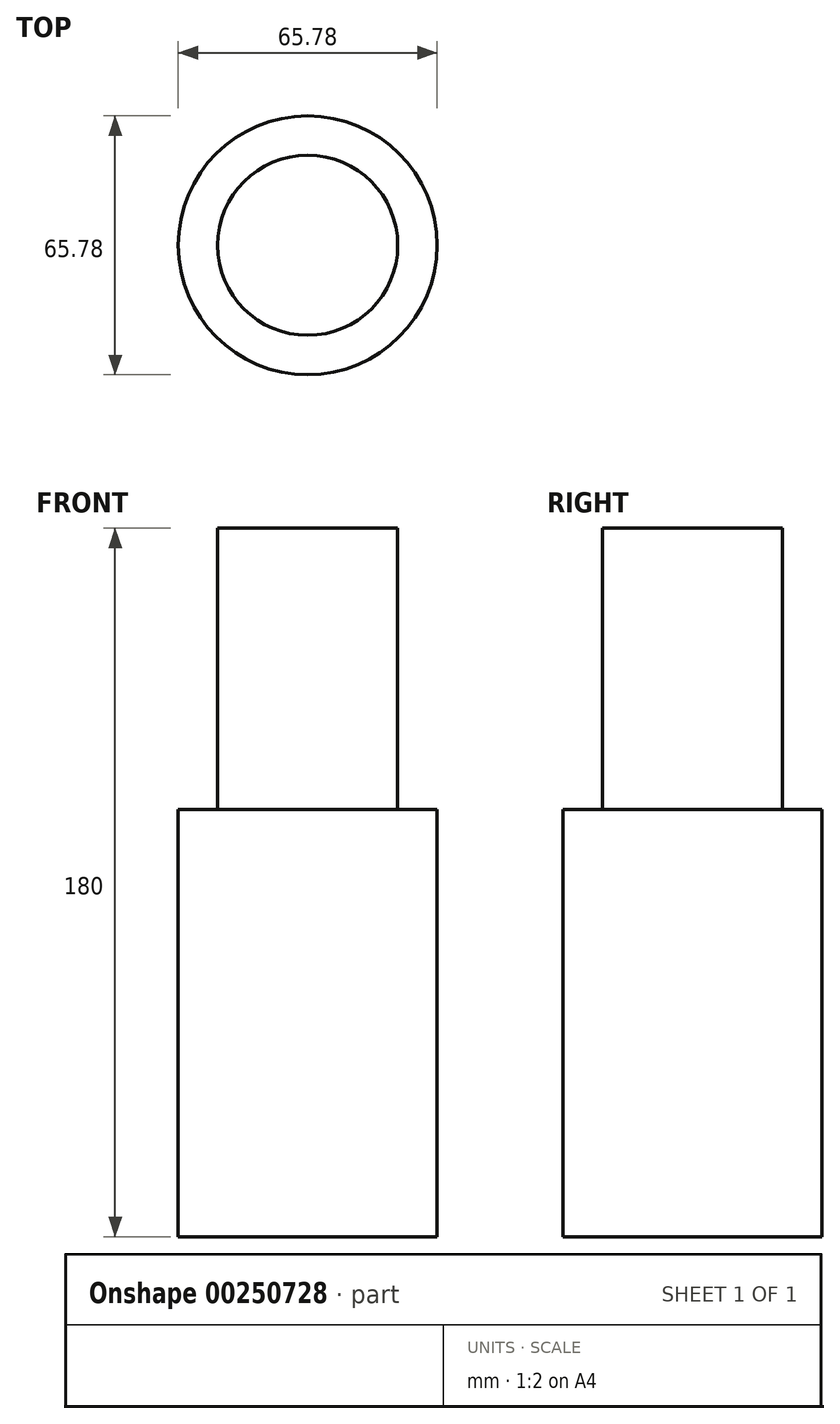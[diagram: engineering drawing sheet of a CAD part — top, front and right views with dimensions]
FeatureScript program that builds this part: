
annotation { "Feature Type Name" : "Feature", "Feature Type Description" : "" }
export const myFeature = defineFeature(function(context is Context, id is Id, definition is map)
    precondition{}
    {
        {
            var Q0;
            Q0=qCreatedBy(makeId("Front.planeOp"),FACE);
            var sketch = newSketch(context, id + "F0", { "sketchPlane" : qUnion([Q0])});
            skLineSegment(sketch, "E0.bottom", {"start": v(-32.89, 50.03) * mm, "end": v(32.89, 50.03) * mm});
            skLineSegment(sketch, "E0.top", {"start": v(-32.89, -58.57) * mm, "end": v(32.89, -58.57) * mm});
            skLineSegment(sketch, "E0.left", {"start": v(-32.89, 50.03) * mm, "end": v(-32.89, -58.57) * mm});
            skLineSegment(sketch, "E0.right", {"start": v(32.89, 50.03) * mm, "end": v(32.89, -58.57) * mm});
            skLineSegment(sketch, "E1", {"start": v(0, 50.03) * mm, "end": v(0, -58.57) * mm});
            skSolve(sketch);
        }
        {
            var Q0;
            {var subQ0=sQuery(id+"F0.wireOp",EDGE,"E0.left");Q0=makeQuery(id+"F0.imprint","IMPRINT",FACE,{"disambiguationData":[TD([[makeQuery(id+"F0.imprint","IMPRINT",EDGE,{"derivedFrom":subQ0}),1.0]])]});}
            var Q1;
            Q1=sQuery(id+"F0.wireOp",EDGE,"E1");
            revolve(context, id + "F1", {"entities" : qUnion([Q0]), "axis" : qUnion([Q1]), "revolveType" : RevolveType.FULL});
        }
        {
            var Q0;
            Q0=makeQuery(id+"F1.opRevolve","SWEPT_FACE",FACE,{"disambiguationData":[OSD([sQuery(id+"F0.wireOp",EDGE,"E0.bottom")])]});
            shell(context, id + "F2", {"entities" : qUnion([Q0]), "thickness" : 10 * mm});
        }
        {
            var Q0;
            Q0=makeQuery(id+"F2.opShell","OFFSET_FACE",FACE,{"disambiguationData":[OSD([sQuery(id+"F0.wireOp",EDGE,"E0.top")])]});
            extrude(context, id + "F3", {"entities" : qUnion([Q0]), "operationType" : NewBodyOperationType.ADD, "depth" : 170 * mm});
        }
    });
